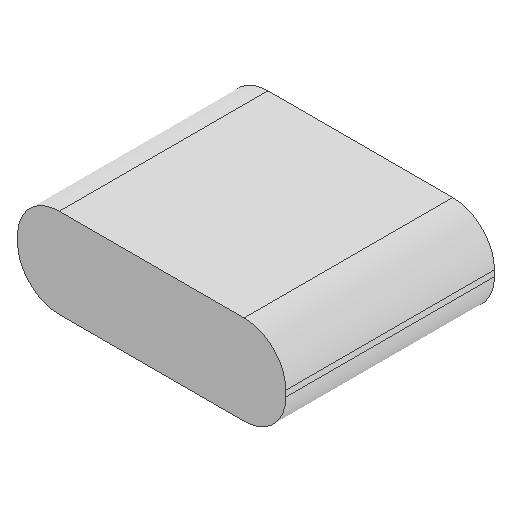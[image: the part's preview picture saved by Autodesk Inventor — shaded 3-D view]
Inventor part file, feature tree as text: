
AUTODESK INVENTOR PART (.ipt)
format: ipt  version: 2025.2 (Build 292293000, 293)  size: 144,384 bytes
history: native  units: mm
features: extrude x2, fillet x2, sketch x2, projected_geometry x1
ambient origin geometry x8: Origin, YZ Plane, XZ Plane, XY Plane, X Axis, Y Axis, Z Axis, Center Point
bodies: Solid1 (feature_tree)
feature tree (7):
  extrude  "Extrusion1"  Depth=3.0mm
  fillet  "Fillet1"  Radius=7.0mm
  extrude  "Extrusion2"  Depth=0.2mm
  fillet  "Fillet2"  Radius=7.0mm
  sketch  "Sketch1"  dims[d0=9.0mm d1=3.0mm d2=7.0mm d3=0.0mm]
  sketch  "Sketch2"  dims[d4=1.4mm d5=0.2mm d6=7.0mm d7=0.7mm d8=6.0mm d9=0.0mm d10=0.3mm]
  projected_geometry  "Projected Loop1"
